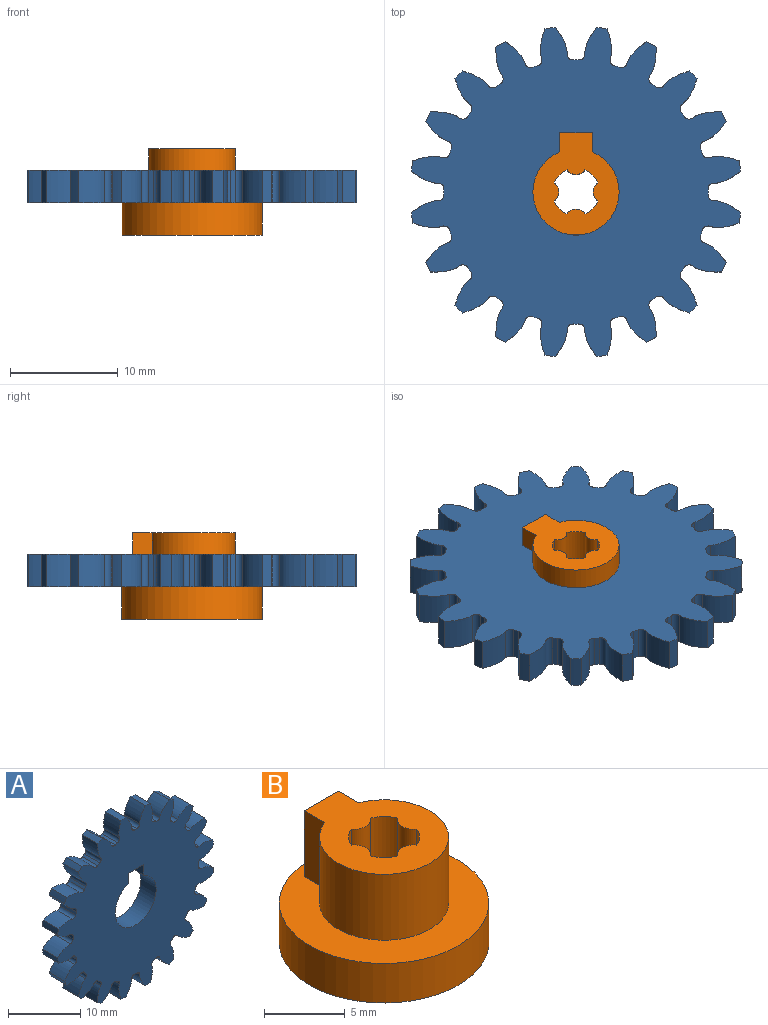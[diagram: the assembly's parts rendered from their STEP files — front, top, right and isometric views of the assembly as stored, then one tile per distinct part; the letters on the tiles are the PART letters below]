
ASSEMBLY  parts=2 mates=1
PART A: 126 faces, bbox 30.6x3x30.6 mm
  f0: cylinder r=15.4mm len=3mm, axis (0,1,0), area 2.9mm2, adj f19,f25,f76,f123
  f1: cylinder r=15.4mm len=3mm, axis (0,1,0), area 2.9mm2, adj f19,f25,f118,f121
  f2: cylinder r=15.4mm len=3mm, axis (0,1,0), area 2.9mm2, adj f19,f25,f113,f116
  f3: cylinder r=15.4mm len=3mm, axis (0,1,0), area 2.9mm2, adj f19,f25,f108,f111
  f4: cylinder r=15.4mm len=3mm, axis (0,1,0), area 2.9mm2, adj f19,f25,f103,f106
  f5: cylinder r=15.4mm len=3mm, axis (0,1,0), area 2.9mm2, adj f19,f25,f98,f101
  f6: cylinder r=15.4mm len=3mm, axis (0,1,0), area 2.9mm2, adj f19,f25,f93,f96
  f7: cylinder r=15.4mm len=3mm, axis (0,1,0), area 2.9mm2, adj f19,f25,f88,f91
  f8: cylinder r=15.4mm len=3mm, axis (0,1,0), area 2.9mm2, adj f19,f25,f71,f83
  f9: cylinder r=15.4mm len=3mm, axis (0,1,0), area 2.9mm2, adj f19,f25,f78,f81
  f10: cylinder r=15.4mm len=3mm, axis (0,1,0), area 2.9mm2, adj f19,f25,f66,f73
  f11: cylinder r=15.4mm len=3mm, axis (0,1,0), area 2.9mm2, adj f19,f25,f46,f68
  f12: cylinder r=15.4mm len=3mm, axis (0,1,0), area 2.9mm2, adj f19,f25,f26,f63
  f13: cylinder r=15.4mm len=3mm, axis (0,1,0), area 2.9mm2, adj f19,f25,f58,f61
  f14: cylinder r=15.4mm len=3mm, axis (0,1,0), area 2.9mm2, adj f19,f25,f53,f56
  f15: cylinder r=15.4mm len=3mm, axis (0,1,0), area 2.9mm2, adj f19,f25,f48,f51
  f16: cylinder r=15.4mm len=3mm, axis (0,1,0), area 2.9mm2, adj f19,f25,f36,f43
  f17: cylinder r=15.4mm len=3mm, axis (0,1,0), area 2.9mm2, adj f19,f25,f38,f86
  f18: cylinder r=15.4mm len=3mm, axis (0,1,0), area 2.9mm2, adj f19,f25,f33,f41
  f19: plane 30.58x30.58mm, normal (0,-1,0), area 548.3mm2, adj f0,f1,f2,f3,f4,f5,f6,f7
  f20: plane 3x1.79mm, normal (-1,0,0), area 5.4mm2, adj f19,f21,f23,f25
  f21: cylinder r=4mm len=8mm, axis (0,1,0), area 66.2mm2, adj f19,f20,f22,f25
  f22: plane 3x1.79mm, normal (1,0,0), area 5.4mm2, adj f19,f21,f23,f25
  f23: plane 3x3mm, normal (0,0,-1), area 9mm2, adj f19,f20,f22,f25
  f24: cylinder r=15.4mm len=3mm, axis (0,1,0), area 2.9mm2, adj f19,f25,f28,f31
  f25: plane 30.58x30.58mm, normal (0,1,0), area 548.3mm2, adj f0,f1,f2,f3,f4,f5,f6,f7
  f26: extruded ~3x2.51mm, area 8.4mm2, adj f12,f19,f25,f29
  f27: cylinder r=12.25mm len=3mm, axis (0,1,0), area 1.5mm2, adj f19,f25,f29,f30
  f28: extruded ~3x2.51mm, area 8.4mm2, adj f19,f24,f25,f30
  f29: cylinder r=0.55mm len=3mm, axis (0,1,0), area 2.5mm2, adj f19,f25,f26,f27
  f30: cylinder r=0.55mm len=3mm, axis (0,1,0), area 2.5mm2, adj f19,f25,f27,f28
  f31: extruded ~3x2.73mm, area 8.4mm2, adj f19,f24,f25,f34
  f32: cylinder r=12.25mm len=3mm, axis (0,1,0), area 1.5mm2, adj f19,f25,f34,f35
  f33: extruded ~3x2.04mm, area 8.4mm2, adj f18,f19,f25,f35
  f34: cylinder r=0.55mm len=3mm, axis (0,1,0), area 2.5mm2, adj f19,f25,f31,f32
  f35: cylinder r=0.55mm len=3mm, axis (0,1,0), area 2.5mm2, adj f19,f25,f32,f33
  f36: extruded ~3x2.38mm, area 8.4mm2, adj f16,f19,f25,f39
  f37: cylinder r=12.25mm len=3mm, axis (0,1,0), area 1.5mm2, adj f19,f25,f39,f40
  f38: extruded ~3x2.69mm, area 8.4mm2, adj f17,f19,f25,f40
  f39: cylinder r=0.55mm len=3mm, axis (0,1,0), area 2.5mm2, adj f19,f25,f36,f37
  f40: cylinder r=0.55mm len=3mm, axis (0,1,0), area 2.5mm2, adj f19,f25,f37,f38
  f41: extruded ~3x2.69mm, area 8.4mm2, adj f18,f19,f25,f44
  f42: cylinder r=12.25mm len=3mm, axis (0,1,0), area 1.5mm2, adj f19,f25,f44,f45
  f43: extruded ~3x2.38mm, area 8.4mm2, adj f16,f19,f25,f45
  f44: cylinder r=0.55mm len=3mm, axis (0,1,0), area 2.5mm2, adj f19,f25,f41,f42
  f45: cylinder r=0.55mm len=3mm, axis (0,1,0), area 2.5mm2, adj f19,f25,f42,f43
  f46: extruded ~3x2.73mm, area 8.4mm2, adj f11,f19,f25,f49
  f47: cylinder r=12.25mm len=3mm, axis (0,1,0), area 1.5mm2, adj f19,f25,f49,f50
  f48: extruded ~3x2.04mm, area 8.4mm2, adj f15,f19,f25,f50
  f49: cylinder r=0.55mm len=3mm, axis (0,1,0), area 2.5mm2, adj f19,f25,f46,f47
  f50: cylinder r=0.55mm len=3mm, axis (0,1,0), area 2.5mm2, adj f19,f25,f47,f48
  f51: extruded ~3x2.69mm, area 8.4mm2, adj f15,f19,f25,f54
  f52: cylinder r=12.25mm len=3mm, axis (0,1,0), area 1.5mm2, adj f19,f25,f54,f55
  f53: extruded ~3x2.38mm, area 8.4mm2, adj f14,f19,f25,f55
  f54: cylinder r=0.55mm len=3mm, axis (0,1,0), area 2.5mm2, adj f19,f25,f51,f52
  f55: cylinder r=0.55mm len=3mm, axis (0,1,0), area 2.5mm2, adj f19,f25,f52,f53
  f56: extruded ~3x2.38mm, area 8.4mm2, adj f14,f19,f25,f59
  f57: cylinder r=12.25mm len=3mm, axis (0,1,0), area 1.5mm2, adj f19,f25,f59,f60
  f58: extruded ~3x2.69mm, area 8.4mm2, adj f13,f19,f25,f60
  f59: cylinder r=0.55mm len=3mm, axis (0,1,0), area 2.5mm2, adj f19,f25,f56,f57
  f60: cylinder r=0.55mm len=3mm, axis (0,1,0), area 2.5mm2, adj f19,f25,f57,f58
  f61: extruded ~3x2.04mm, area 8.4mm2, adj f13,f19,f25,f64
  f62: cylinder r=12.25mm len=3mm, axis (0,1,0), area 1.5mm2, adj f19,f25,f64,f65
  f63: extruded ~3x2.73mm, area 8.4mm2, adj f12,f19,f25,f65
  f64: cylinder r=0.55mm len=3mm, axis (0,1,0), area 2.5mm2, adj f19,f25,f61,f62
  f65: cylinder r=0.55mm len=3mm, axis (0,1,0), area 2.5mm2, adj f19,f25,f62,f63
  f66: extruded ~3x2.51mm, area 8.4mm2, adj f10,f19,f25,f69
  f67: cylinder r=12.25mm len=3mm, axis (0,1,0), area 1.5mm2, adj f19,f25,f69,f70
  f68: extruded ~3x2.51mm, area 8.4mm2, adj f11,f19,f25,f70
  f69: cylinder r=0.55mm len=3mm, axis (0,1,0), area 2.5mm2, adj f19,f25,f66,f67
  f70: cylinder r=0.55mm len=3mm, axis (0,1,0), area 2.5mm2, adj f19,f25,f67,f68
  f71: extruded ~3x2.04mm, area 8.4mm2, adj f8,f19,f25,f74
  f72: cylinder r=12.25mm len=3mm, axis (0,1,0), area 1.5mm2, adj f19,f25,f74,f75
  f73: extruded ~3x2.73mm, area 8.4mm2, adj f10,f19,f25,f75
  f74: cylinder r=0.55mm len=3mm, axis (0,1,0), area 2.5mm2, adj f19,f25,f71,f72
  f75: cylinder r=0.55mm len=3mm, axis (0,1,0), area 2.5mm2, adj f19,f25,f72,f73
  f76: extruded ~3x2.69mm, area 8.4mm2, adj f0,f19,f25,f79
  f77: cylinder r=12.25mm len=3mm, axis (0,1,0), area 1.5mm2, adj f19,f25,f79,f80
  f78: extruded ~3x2.38mm, area 8.4mm2, adj f9,f19,f25,f80
  f79: cylinder r=0.55mm len=3mm, axis (0,1,0), area 2.5mm2, adj f19,f25,f76,f77
  f80: cylinder r=0.55mm len=3mm, axis (0,1,0), area 2.5mm2, adj f19,f25,f77,f78
  f81: extruded ~3x2.38mm, area 8.4mm2, adj f9,f19,f25,f84
  f82: cylinder r=12.25mm len=3mm, axis (0,1,0), area 1.5mm2, adj f19,f25,f84,f85
  f83: extruded ~3x2.69mm, area 8.4mm2, adj f8,f19,f25,f85
  f84: cylinder r=0.55mm len=3mm, axis (0,1,0), area 2.5mm2, adj f19,f25,f81,f82
  f85: cylinder r=0.55mm len=3mm, axis (0,1,0), area 2.5mm2, adj f19,f25,f82,f83
  f86: extruded ~3x2.04mm, area 8.4mm2, adj f17,f19,f25,f89
  f87: cylinder r=12.25mm len=3mm, axis (0,1,0), area 1.5mm2, adj f19,f25,f89,f90
  f88: extruded ~3x2.73mm, area 8.4mm2, adj f7,f19,f25,f90
  f89: cylinder r=0.55mm len=3mm, axis (0,1,0), area 2.5mm2, adj f19,f25,f86,f87
  f90: cylinder r=0.55mm len=3mm, axis (0,1,0), area 2.5mm2, adj f19,f25,f87,f88
  f91: extruded ~3x2.51mm, area 8.4mm2, adj f7,f19,f25,f94
  f92: cylinder r=12.25mm len=3mm, axis (0,1,0), area 1.5mm2, adj f19,f25,f94,f95
  f93: extruded ~3x2.51mm, area 8.4mm2, adj f6,f19,f25,f95
  f94: cylinder r=0.55mm len=3mm, axis (0,1,0), area 2.5mm2, adj f19,f25,f91,f92
  f95: cylinder r=0.55mm len=3mm, axis (0,1,0), area 2.5mm2, adj f19,f25,f92,f93
  f96: extruded ~3x2.73mm, area 8.4mm2, adj f6,f19,f25,f99
  f97: cylinder r=12.25mm len=3mm, axis (0,1,0), area 1.5mm2, adj f19,f25,f99,f100
  f98: extruded ~3x2.04mm, area 8.4mm2, adj f5,f19,f25,f100
  f99: cylinder r=0.55mm len=3mm, axis (0,1,0), area 2.5mm2, adj f19,f25,f96,f97
  f100: cylinder r=0.55mm len=3mm, axis (0,1,0), area 2.5mm2, adj f19,f25,f97,f98
  f101: extruded ~3x2.69mm, area 8.4mm2, adj f5,f19,f25,f104
  f102: cylinder r=12.25mm len=3mm, axis (0,1,0), area 1.5mm2, adj f19,f25,f104,f105
  f103: extruded ~3x2.38mm, area 8.4mm2, adj f4,f19,f25,f105
  f104: cylinder r=0.55mm len=3mm, axis (0,1,0), area 2.5mm2, adj f19,f25,f101,f102
  f105: cylinder r=0.55mm len=3mm, axis (0,1,0), area 2.5mm2, adj f19,f25,f102,f103
  f106: extruded ~3x2.38mm, area 8.4mm2, adj f4,f19,f25,f109
  f107: cylinder r=12.25mm len=3mm, axis (0,1,0), area 1.5mm2, adj f19,f25,f109,f110
  f108: extruded ~3x2.69mm, area 8.4mm2, adj f3,f19,f25,f110
  f109: cylinder r=0.55mm len=3mm, axis (0,1,0), area 2.5mm2, adj f19,f25,f106,f107
  f110: cylinder r=0.55mm len=3mm, axis (0,1,0), area 2.5mm2, adj f19,f25,f107,f108
  f111: extruded ~3x2.04mm, area 8.4mm2, adj f3,f19,f25,f114
  f112: cylinder r=12.25mm len=3mm, axis (0,1,0), area 1.5mm2, adj f19,f25,f114,f115
  f113: extruded ~3x2.73mm, area 8.4mm2, adj f2,f19,f25,f115
  f114: cylinder r=0.55mm len=3mm, axis (0,1,0), area 2.5mm2, adj f19,f25,f111,f112
  f115: cylinder r=0.55mm len=3mm, axis (0,1,0), area 2.5mm2, adj f19,f25,f112,f113
  f116: extruded ~3x2.51mm, area 8.4mm2, adj f2,f19,f25,f119
  f117: cylinder r=12.25mm len=3mm, axis (0,1,0), area 1.5mm2, adj f19,f25,f119,f120
  f118: extruded ~3x2.51mm, area 8.4mm2, adj f1,f19,f25,f120
  f119: cylinder r=0.55mm len=3mm, axis (0,1,0), area 2.5mm2, adj f19,f25,f116,f117
  f120: cylinder r=0.55mm len=3mm, axis (0,1,0), area 2.5mm2, adj f19,f25,f117,f118
  f121: extruded ~3x2.73mm, area 8.4mm2, adj f1,f19,f25,f124
  f122: cylinder r=12.25mm len=3mm, axis (0,1,0), area 1.5mm2, adj f19,f25,f124,f125
  f123: extruded ~3x2.04mm, area 8.4mm2, adj f0,f19,f25,f125
  f124: cylinder r=0.55mm len=3mm, axis (0,1,0), area 2.5mm2, adj f19,f25,f121,f122
  f125: cylinder r=0.55mm len=3mm, axis (0,1,0), area 2.5mm2, adj f19,f25,f122,f123
PART B: 18 faces, bbox 13x13x8 mm
  f0: cylinder r=2.2mm len=6mm, axis (0,0,-1), area 10.6mm2, adj f11,f13,f14,f17
  f1: cylinder r=2.2mm len=6mm, axis (0,0,-1), area 10.6mm2, adj f11,f13,f16,f17
  f2: cylinder r=2.2mm len=6mm, axis (0,0,-1), area 10.6mm2, adj f11,f13,f15,f16
  f3: cylinder r=2.2mm len=6mm, axis (0,0,-1), area 10.6mm2, adj f11,f13,f14,f15
  f4: cylinder r=6.5mm len=13mm, axis (0,0,-1), area 122.5mm2, adj f5,f6
  f5: plane 13x13mm, normal (0,0,1), area 77.7mm2, adj f4,f7,f8,f9,f10
  f6: plane 13x13mm, normal (0,0,-1), area 99.5mm2, adj f4,f12
  f7: cylinder r=4mm len=8mm, axis (0,0,-1), area 110.3mm2, adj f5,f8,f10,f11
  f8: plane 5x1.79mm, normal (1,0,0), area 9mm2, adj f5,f7,f9,f11
  f9: plane 5x3mm, normal (0,1,0), area 15mm2, adj f5,f8,f10,f11
  f10: plane 5x1.79mm, normal (-1,0,0), area 9mm2, adj f5,f7,f9,f11
  f11: plane 9.5x8mm, normal (0,0,1), area 42.6mm2, adj f0,f1,f2,f3,f7,f8,f9,f10
  f12: cylinder r=3.25mm len=6.5mm, axis (0,0,1), area 40.8mm2, adj f6,f13
  f13: plane 6.5x6.5mm, normal (0,0,-1), area 20.7mm2, adj f0,f1,f2,f3,f12,f14,f15,f16
  f14: cylinder r=1mm len=6mm, axis (0,0,1), area 11.7mm2, adj f0,f3,f11,f13
  f15: cylinder r=1mm len=6mm, axis (0,0,1), area 11.7mm2, adj f2,f3,f11,f13
  f16: cylinder r=1mm len=6mm, axis (0,0,1), area 11.7mm2, adj f1,f2,f11,f13
  f17: cylinder r=1mm len=6mm, axis (0,0,1), area 11.7mm2, adj f0,f1,f11,f13
PLACE A rot(axis=(0,-0.71,-0.71),180deg) t=(-8.43,4.08,31.21)mm
PLACE B t=(-8.43,4.08,11.21)mm fixed
MATE fastened A.f23 <-> B.f9  axis (0,-1,0) through (-6.93,9.58,28.21)mm
